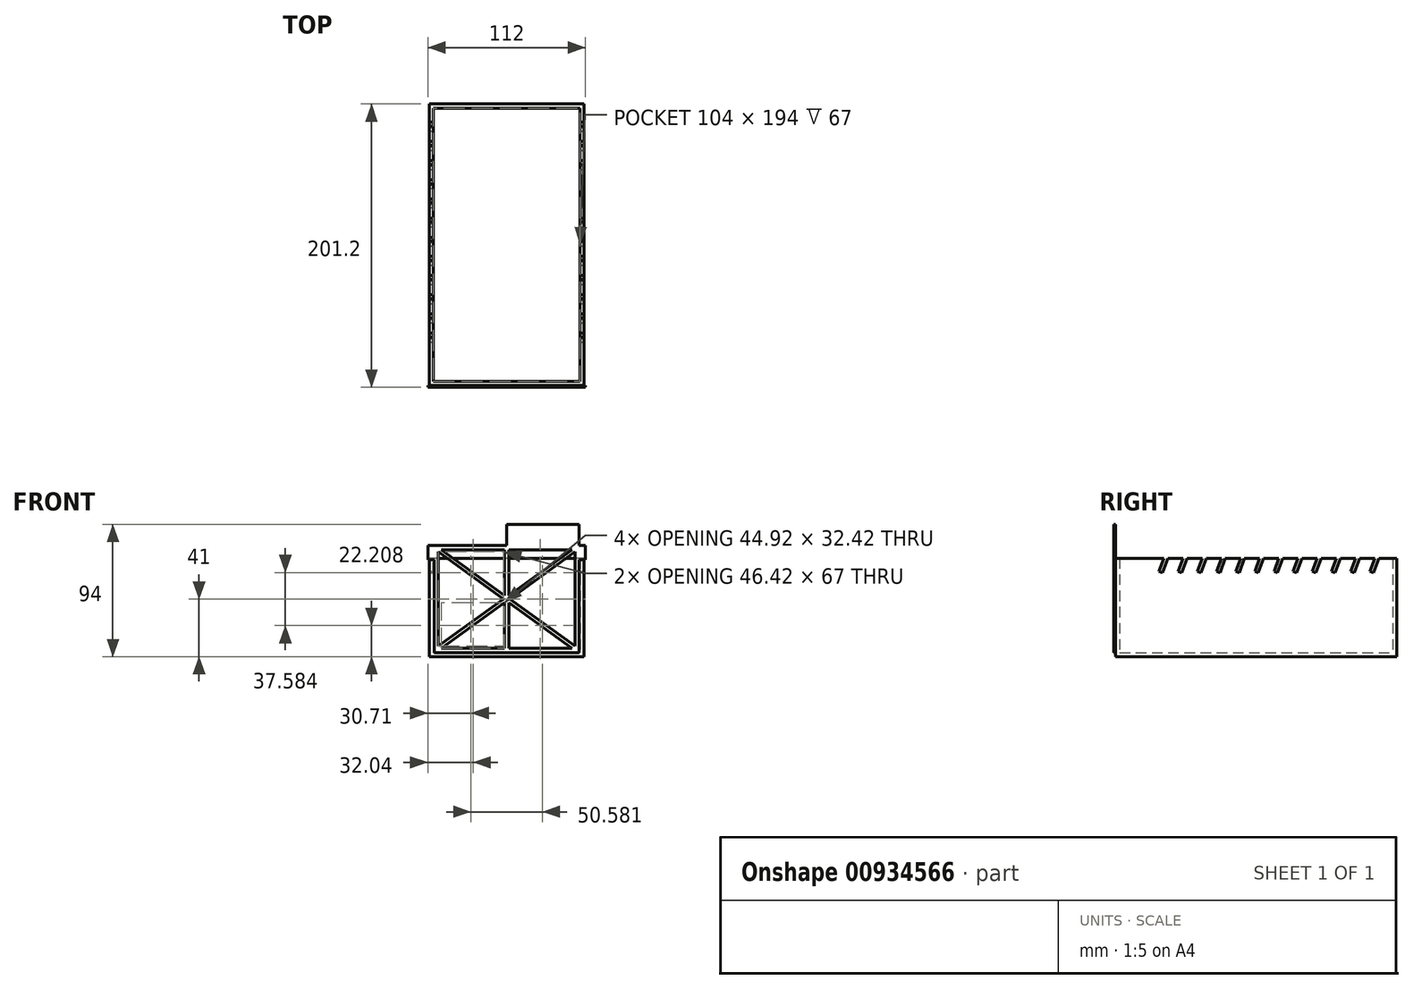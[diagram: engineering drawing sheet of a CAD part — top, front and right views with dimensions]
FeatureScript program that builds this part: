
annotation { "Feature Type Name" : "Feature", "Feature Type Description" : "" }
export const myFeature = defineFeature(function(context is Context, id is Id, definition is map)
    precondition{}
    {
        {
            var Q0;
            Q0=qCreatedBy(makeId("Top.planeOp"),FACE);
            var sketch = newSketch(context, id + "F0", { "sketchPlane" : qUnion([Q0])});
            skLineSegment(sketch, "E0.bottom", {"start": v(0, 0) * mm, "end": v(-110, 0) * mm});
            skLineSegment(sketch, "E0.top", {"start": v(0, 200) * mm, "end": v(-110, 200) * mm});
            skLineSegment(sketch, "E0.left", {"start": v(0, 0) * mm, "end": v(0, 200) * mm});
            skLineSegment(sketch, "E0.right", {"start": v(-110, 0) * mm, "end": v(-110, 200) * mm});
            skSolve(sketch);
        }
        {
            var Q0;
            Q0=makeQuery(id+"F0.imprint","IMPRINT",FACE,{"disambiguationData":[TD([[makeQuery(id+"F0.imprint","IMPRINT",EDGE,{"derivedFrom":sQuery(id+"F0.wireOp",EDGE,"E0.bottom")}),-1.0]])]});
            extrude(context, id + "F1", {"entities" : qUnion([Q0]), "depth" : 70 * mm, "offsetDistance" : 25 * mm});
        }
        {
            var Q0;
            Q0=makeQuery(id+"F1.opExtrude","CAP_FACE",FACE,{"disambiguationData":[OSD([sQuery(id+"F0.wireOp",EDGE,"E0.bottom"),sQuery(id+"F0.wireOp",EDGE,"E0.top"),sQuery(id+"F0.wireOp",EDGE,"E0.left"),sQuery(id+"F0.wireOp",EDGE,"E0.right")])],"isStart":false});
            shell(context, id + "F2", {"entities" : qUnion([Q0]), "thickness" : 3 * mm});
        }
        {
            var Q0;
            Q0=makeQuery(id+"F1.opExtrude","SWEPT_FACE",FACE,{"disambiguationData":[OSD([sQuery(id+"F0.wireOp",EDGE,"E0.bottom")])]});
            var sketch = newSketch(context, id + "F3", { "sketchPlane" : qUnion([Q0])});
            skLineSegment(sketch, "E1.bottom", {"start": v(-106.5, 79) * mm, "end": v(-55, 79) * mm});
            skLineSegment(sketch, "E1.top", {"start": v(-106.5, 3) * mm, "end": v(-3.5, 3) * mm});
            skLineSegment(sketch, "E1.left", {"start": v(-106.5, 69) * mm, "end": v(-106.5, 3) * mm});
            skLineSegment(sketch, "E1.right", {"start": v(-3.5, 69) * mm, "end": v(-3.5, 3) * mm});
            skPoint(sketch, "E2.oppositeSnap0", {"position": v(-55, 79) * mm});
            skLineSegment(sketch, "E2.top", {"start": v(-3.5, 94) * mm, "end": v(-55, 94) * mm});
            skLineSegment(sketch, "E2.left", {"start": v(-3.5, 79) * mm, "end": v(-3.5, 94) * mm});
            skLineSegment(sketch, "E2.right", {"start": v(-55, 79) * mm, "end": v(-55, 94) * mm});
            skLineSegment(sketch, "E3.1", {"start": v(-6.5, 76) * mm, "end": v(-6.5, 6) * mm});
            skLineSegment(sketch, "E3.3", {"start": v(-103.5, 76) * mm, "end": v(-6.5, 76) * mm});
            skLineSegment(sketch, "E3.4", {"start": v(-103.5, 76) * mm, "end": v(-103.5, 6) * mm});
            skLineSegment(sketch, "E3.5", {"start": v(-6.5, 91) * mm, "end": v(-52.5, 91) * mm, "construction": true});
            skLineSegment(sketch, "E3.6", {"start": v(-103.5, 6) * mm, "end": v(-6.5, 6) * mm});
            skLineSegment(sketch, "E4", {"start": v(-103.5, 76) * mm, "end": v(-6.5, 6) * mm, "construction": true});
            skLineSegment(sketch, "E5", {"start": v(-6.5, 76) * mm, "end": v(-103.5, 6) * mm, "construction": true});
            skLineSegment(sketch, "E6.0.left", {"start": v(-6.5, 74.5) * mm, "end": v(-101.42, 6) * mm});
            skLineSegment(sketch, "E6.0.right", {"start": v(-8.58, 76) * mm, "end": v(-103.5, 7.5) * mm});
            skLineSegment(sketch, "E7.0.left", {"start": v(-101.42, 76) * mm, "end": v(-6.5, 7.5) * mm});
            skLineSegment(sketch, "E7.0.right", {"start": v(-103.5, 74.5) * mm, "end": v(-8.58, 6) * mm});
            skLineSegment(sketch, "E8", {"start": v(-55, 76) * mm, "end": v(-55, 6) * mm, "construction": true});
            skLineSegment(sketch, "E9.0.left", {"start": v(-53.5, 76) * mm, "end": v(-53.5, 6) * mm});
            skLineSegment(sketch, "E9.0.right", {"start": v(-56.5, 76) * mm, "end": v(-56.5, 6) * mm});
            skLineSegment(sketch, "E10.bottom", {"start": v(-106.5, 79) * mm, "end": v(-111, 79) * mm});
            skLineSegment(sketch, "E10.top", {"start": v(-106.5, 69) * mm, "end": v(-111, 69) * mm});
            skLineSegment(sketch, "E10.right", {"start": v(-111, 79) * mm, "end": v(-111, 69) * mm});
            skLineSegment(sketch, "E11.MirrorCS", {"start": v(-3.5, 69) * mm, "end": v(1, 69) * mm});
            skLineSegment(sketch, "E12.MirrorCS", {"start": v(-3.5, 79) * mm, "end": v(1, 79) * mm});
            skLineSegment(sketch, "E13.MirrorCS", {"start": v(1, 79) * mm, "end": v(1, 69) * mm});
            skSolve(sketch);
        }
        {
            var Q0;
            Q0=makeQuery(id+"F1.opExtrude","SWEPT_FACE",FACE,{"disambiguationData":[OSD([sQuery(id+"F0.wireOp",EDGE,"E0.left")])]});
            var sketch = newSketch(context, id + "F4", { "sketchPlane" : qUnion([Q0])});
            skLineSegment(sketch, "E14", {"start": v(187, 70) * mm, "end": v(183.24, 59.66) * mm});
            skLineSegment(sketch, "E15", {"start": v(180.8, 60.55) * mm, "end": v(184.23, 70) * mm});
            skLineSegment(sketch, "E16", {"start": v(187, 70) * mm, "end": v(184.23, 70) * mm});
            skLineSegment(sketch, "E17", {"start": v(183.24, 59.66) * mm, "end": v(180.8, 60.55) * mm});
            skLineSegment(sketch, "E18.1.0.0", {"start": v(167.18, 60.55) * mm, "end": v(170.62, 70) * mm});
            skLineSegment(sketch, "E18.1.0.1", {"start": v(173.38, 70) * mm, "end": v(170.62, 70) * mm});
            skLineSegment(sketch, "E18.1.0.2", {"start": v(173.38, 70) * mm, "end": v(169.62, 59.66) * mm});
            skLineSegment(sketch, "E18.1.0.3", {"start": v(169.62, 59.66) * mm, "end": v(167.18, 60.55) * mm});
            skLineSegment(sketch, "E18.2.0.0", {"start": v(153.56, 60.55) * mm, "end": v(157, 70) * mm});
            skLineSegment(sketch, "E18.2.0.1", {"start": v(159.76, 70) * mm, "end": v(157, 70) * mm});
            skLineSegment(sketch, "E18.2.0.2", {"start": v(159.76, 70) * mm, "end": v(156, 59.66) * mm});
            skLineSegment(sketch, "E18.2.0.3", {"start": v(156, 59.66) * mm, "end": v(153.56, 60.55) * mm});
            skLineSegment(sketch, "E18.3.0.0", {"start": v(139.94, 60.55) * mm, "end": v(143.38, 70) * mm});
            skLineSegment(sketch, "E18.3.0.1", {"start": v(146.15, 70) * mm, "end": v(143.38, 70) * mm});
            skLineSegment(sketch, "E18.3.0.2", {"start": v(146.15, 70) * mm, "end": v(142.38, 59.66) * mm});
            skLineSegment(sketch, "E18.3.0.3", {"start": v(142.38, 59.66) * mm, "end": v(139.94, 60.55) * mm});
            skLineSegment(sketch, "E18.4.0.0", {"start": v(126.32, 60.55) * mm, "end": v(129.76, 70) * mm});
            skLineSegment(sketch, "E18.4.0.1", {"start": v(132.53, 70) * mm, "end": v(129.76, 70) * mm});
            skLineSegment(sketch, "E18.4.0.2", {"start": v(132.53, 70) * mm, "end": v(128.77, 59.66) * mm});
            skLineSegment(sketch, "E18.4.0.3", {"start": v(128.77, 59.66) * mm, "end": v(126.32, 60.55) * mm});
            skLineSegment(sketch, "E18.5.0.0", {"start": v(112.7, 60.55) * mm, "end": v(116.14, 70) * mm});
            skLineSegment(sketch, "E18.5.0.1", {"start": v(118.91, 70) * mm, "end": v(116.14, 70) * mm});
            skLineSegment(sketch, "E18.5.0.2", {"start": v(118.91, 70) * mm, "end": v(115.15, 59.66) * mm});
            skLineSegment(sketch, "E18.5.0.3", {"start": v(115.15, 59.66) * mm, "end": v(112.7, 60.55) * mm});
            skLineSegment(sketch, "E18.6.0.0", {"start": v(99.09, 60.55) * mm, "end": v(102.53, 70) * mm});
            skLineSegment(sketch, "E18.6.0.1", {"start": v(105.3, 70) * mm, "end": v(102.53, 70) * mm});
            skLineSegment(sketch, "E18.6.0.2", {"start": v(105.3, 70) * mm, "end": v(101.53, 59.66) * mm});
            skLineSegment(sketch, "E18.6.0.3", {"start": v(101.53, 59.66) * mm, "end": v(99.09, 60.55) * mm});
            skLineSegment(sketch, "E18.direction1", {"start": v(180.8, 60.55) * mm, "end": v(167.18, 60.55) * mm, "construction": true});
            skLineSegment(sketch, "E19.0.7.0", {"start": v(85.47, 60.55) * mm, "end": v(88.9, 70) * mm});
            skLineSegment(sketch, "E19.3.7.0", {"start": v(91.68, 70) * mm, "end": v(88.9, 70) * mm});
            skLineSegment(sketch, "E19.6.7.0", {"start": v(91.68, 70) * mm, "end": v(87.91, 59.66) * mm});
            skLineSegment(sketch, "E19.9.7.0", {"start": v(87.91, 59.66) * mm, "end": v(85.47, 60.55) * mm});
            skLineSegment(sketch, "E19.0.8.0", {"start": v(71.85, 60.55) * mm, "end": v(75.3, 70) * mm});
            skLineSegment(sketch, "E19.3.8.0", {"start": v(78.06, 70) * mm, "end": v(75.3, 70) * mm});
            skLineSegment(sketch, "E19.6.8.0", {"start": v(78.06, 70) * mm, "end": v(74.3, 59.66) * mm});
            skLineSegment(sketch, "E19.9.8.0", {"start": v(74.3, 59.66) * mm, "end": v(71.85, 60.55) * mm});
            skLineSegment(sketch, "E19.0.9.0", {"start": v(58.24, 60.55) * mm, "end": v(61.67, 70) * mm});
            skLineSegment(sketch, "E19.3.9.0", {"start": v(64.44, 70) * mm, "end": v(61.67, 70) * mm});
            skLineSegment(sketch, "E19.6.9.0", {"start": v(64.44, 70) * mm, "end": v(60.68, 59.66) * mm});
            skLineSegment(sketch, "E19.9.9.0", {"start": v(60.68, 59.66) * mm, "end": v(58.24, 60.55) * mm});
            skLineSegment(sketch, "E20.0.10.0", {"start": v(44.62, 60.55) * mm, "end": v(48.06, 70) * mm});
            skLineSegment(sketch, "E20.3.10.0", {"start": v(50.82, 70) * mm, "end": v(48.06, 70) * mm});
            skLineSegment(sketch, "E20.6.10.0", {"start": v(50.82, 70) * mm, "end": v(47.06, 59.66) * mm});
            skLineSegment(sketch, "E20.9.10.0", {"start": v(47.06, 59.66) * mm, "end": v(44.62, 60.55) * mm});
            skLineSegment(sketch, "E20.0.11.0", {"start": v(31, 60.55) * mm, "end": v(34.44, 70) * mm});
            skLineSegment(sketch, "E20.3.11.0", {"start": v(37.2, 70) * mm, "end": v(34.44, 70) * mm});
            skLineSegment(sketch, "E20.6.11.0", {"start": v(37.2, 70) * mm, "end": v(33.44, 59.66) * mm});
            skLineSegment(sketch, "E20.9.11.0", {"start": v(33.44, 59.66) * mm, "end": v(31, 60.55) * mm});
            skSolve(sketch);
        }
        {
            var Q0;
            Q0 = qSketchRegion(id + "F4", true);
            extrude(context, id + "F5", {"entities" : qUnion([Q0]), "operationType" : NewBodyOperationType.REMOVE, "endBound" : BoundingType.THROUGH_ALL, "oppositeDirection" : true, "depth" : 25 * mm, "offsetDistance" : 25 * mm});
        }
        {
            var Q0;
            {var subQ9=sQuery(id+"F3.wireOp",EDGE,"E1.bottom");Q0=makeQuery(id+"F3.imprint","IMPRINT",FACE,{"disambiguationData":[TD([[makeQuery(id+"F3.imprint","IMPRINT",EDGE,{"derivedFrom":subQ9}),-1.0]])]});}
            var Q1;
            {var subQ3=sQuery(id+"F3.wireOp",EDGE,"E1.top");Q1=makeQuery(id+"F3.imprint","IMPRINT",FACE,{"disambiguationData":[TD([[makeQuery(id+"F3.imprint","IMPRINT",EDGE,{"derivedFrom":subQ3}),1.0]])]});}
            var Q2;
            {var subQ1=sQuery(id+"F3.wireOp",EDGE,"E3.4");var subQ6=sQuery(id+"F3.wireOp",EDGE,"E3.6");var subQ10=makeQuery(id+"F3.imprint","INTERSECT",VERTEX,{"derivedFrom":[subQ1,subQ6]});Q2=makeQuery(id+"F3.imprint","IMPRINT",FACE,{"disambiguationData":[TD([[makeQuery(id+"F3.imprint","IMPRINT",EDGE,{"disambiguationData":[TD([[subQ10,1.0]])],"derivedFrom":subQ1}),1.0]])]});}
            var Q3;
            {var subQ0=sQuery(id+"F3.wireOp",EDGE,"E7.0.left");var subQ1=sQuery(id+"F3.wireOp",EDGE,"E6.0.right");var subQ2=makeQuery(id+"F3.imprint","INTERSECT",VERTEX,{"derivedFrom":[subQ1,subQ0]});Q3=makeQuery(id+"F3.imprint","IMPRINT",FACE,{"disambiguationData":[TD([[makeQuery(id+"F3.imprint","IMPRINT",EDGE,{"disambiguationData":[TD([[subQ2,-1.0]])],"derivedFrom":subQ1}),-1.0]])]});}
            var Q4;
            {var subQ5=sQuery(id+"F3.wireOp",EDGE,"E7.0.left");var subQ7=sQuery(id+"F3.wireOp",EDGE,"E6.0.left");var subQ8=makeQuery(id+"F3.imprint","INTERSECT",VERTEX,{"derivedFrom":[subQ7,subQ5]});Q4=makeQuery(id+"F3.imprint","IMPRINT",FACE,{"disambiguationData":[TD([[makeQuery(id+"F3.imprint","IMPRINT",EDGE,{"disambiguationData":[TD([[subQ8,1.0]])],"derivedFrom":subQ7}),-1.0]])]});}
            var Q5;
            {var subQ0=sQuery(id+"F3.wireOp",EDGE,"E7.0.left");var subQ1=sQuery(id+"F3.wireOp",EDGE,"E6.0.left");var subQ2=makeQuery(id+"F3.imprint","INTERSECT",VERTEX,{"derivedFrom":[subQ1,subQ0]});Q5=makeQuery(id+"F3.imprint","IMPRINT",FACE,{"disambiguationData":[TD([[makeQuery(id+"F3.imprint","IMPRINT",EDGE,{"disambiguationData":[TD([[subQ2,-1.0]])],"derivedFrom":subQ1}),-1.0]])]});}
            var Q6;
            {var subQ1=sQuery(id+"F3.wireOp",EDGE,"E3.1");var subQ9=sQuery(id+"F3.wireOp",EDGE,"E3.6");var subQ10=makeQuery(id+"F3.imprint","INTERSECT",VERTEX,{"derivedFrom":[subQ1,subQ9]});Q6=makeQuery(id+"F3.imprint","IMPRINT",FACE,{"disambiguationData":[TD([[makeQuery(id+"F3.imprint","IMPRINT",EDGE,{"disambiguationData":[TD([[subQ10,1.0]])],"derivedFrom":subQ1}),-1.0]])]});}
            var Q7;
            {var subQ1=sQuery(id+"F3.wireOp",EDGE,"E3.3");var subQ6=sQuery(id+"F3.wireOp",EDGE,"E3.1");var subQ9=makeQuery(id+"F3.imprint","INTERSECT",VERTEX,{"derivedFrom":[subQ6,subQ1]});Q7=makeQuery(id+"F3.imprint","IMPRINT",FACE,{"disambiguationData":[TD([[makeQuery(id+"F3.imprint","IMPRINT",EDGE,{"disambiguationData":[TD([[subQ9,-1.0]])],"derivedFrom":subQ6}),-1.0]])]});}
            var Q8;
            {var subQ1=sQuery(id+"F3.wireOp",EDGE,"E3.4");var subQ6=sQuery(id+"F3.wireOp",EDGE,"E3.3");var subQ9=makeQuery(id+"F3.imprint","INTERSECT",VERTEX,{"derivedFrom":[subQ6,subQ1]});Q8=makeQuery(id+"F3.imprint","IMPRINT",FACE,{"disambiguationData":[TD([[makeQuery(id+"F3.imprint","IMPRINT",EDGE,{"disambiguationData":[TD([[subQ9,-1.0]])],"derivedFrom":subQ6}),-1.0]])]});}
            var Q9;
            {var subQ0=sQuery(id+"F3.wireOp",EDGE,"E9.0.right");var subQ1=sQuery(id+"F3.wireOp",EDGE,"E6.0.right");var subQ2=makeQuery(id+"F3.imprint","INTERSECT",VERTEX,{"derivedFrom":[subQ1,subQ0]});Q9=makeQuery(id+"F3.imprint","IMPRINT",FACE,{"disambiguationData":[TD([[makeQuery(id+"F3.imprint","IMPRINT",EDGE,{"disambiguationData":[TD([[subQ2,-1.0]])],"derivedFrom":subQ1}),-1.0]])]});}
            var Q10;
            {var subQ5=sQuery(id+"F3.wireOp",EDGE,"E9.0.left");var subQ6=sQuery(id+"F3.wireOp",EDGE,"E6.0.right");var subQ7=makeQuery(id+"F3.imprint","INTERSECT",VERTEX,{"derivedFrom":[subQ6,subQ5]});Q10=makeQuery(id+"F3.imprint","IMPRINT",FACE,{"disambiguationData":[TD([[makeQuery(id+"F3.imprint","IMPRINT",EDGE,{"disambiguationData":[TD([[subQ7,-1.0]])],"derivedFrom":subQ6}),-1.0]])]});}
            var Q11;
            {var subQ0=sQuery(id+"F3.wireOp",EDGE,"E9.0.left");var subQ1=sQuery(id+"F3.wireOp",EDGE,"E3.3");var subQ2=makeQuery(id+"F3.imprint","INTERSECT",VERTEX,{"derivedFrom":[subQ1,subQ0]});Q11=makeQuery(id+"F3.imprint","IMPRINT",FACE,{"disambiguationData":[TD([[makeQuery(id+"F3.imprint","IMPRINT",EDGE,{"disambiguationData":[TD([[subQ2,1.0]])],"derivedFrom":subQ1}),-1.0]])]});}
            var Q12;
            {var subQ0=sQuery(id+"F3.wireOp",EDGE,"E9.0.left");var subQ1=sQuery(id+"F3.wireOp",EDGE,"E3.6");var subQ2=makeQuery(id+"F3.imprint","INTERSECT",VERTEX,{"derivedFrom":[subQ1,subQ0]});Q12=makeQuery(id+"F3.imprint","IMPRINT",FACE,{"disambiguationData":[TD([[makeQuery(id+"F3.imprint","IMPRINT",EDGE,{"disambiguationData":[TD([[subQ2,1.0]])],"derivedFrom":subQ1}),1.0]])]});}
            var Q13;
            {var subQ1=sQuery(id+"F3.wireOp",EDGE,"E6.0.left");var subQ8=sQuery(id+"F3.wireOp",EDGE,"E9.0.left");var subQ11=makeQuery(id+"F3.imprint","INTERSECT",VERTEX,{"derivedFrom":[subQ1,subQ8]});Q13=makeQuery(id+"F3.imprint","IMPRINT",FACE,{"disambiguationData":[TD([[makeQuery(id+"F3.imprint","IMPRINT",EDGE,{"disambiguationData":[TD([[subQ11,-1.0]])],"derivedFrom":subQ1}),-1.0]])]});}
            var Q14;
            {var subQ0=sQuery(id+"F3.wireOp",EDGE,"E9.0.left");var subQ1=sQuery(id+"F3.wireOp",EDGE,"E6.0.left");var subQ2=makeQuery(id+"F3.imprint","INTERSECT",VERTEX,{"derivedFrom":[subQ1,subQ0]});Q14=makeQuery(id+"F3.imprint","IMPRINT",FACE,{"disambiguationData":[TD([[makeQuery(id+"F3.imprint","IMPRINT",EDGE,{"disambiguationData":[TD([[subQ2,-1.0]])],"derivedFrom":subQ1}),1.0]])]});}
            var Q15;
            {var subQ0=sQuery(id+"F3.wireOp",EDGE,"E9.0.left");var subQ1=sQuery(id+"F3.wireOp",EDGE,"E6.0.right");var subQ2=makeQuery(id+"F3.imprint","INTERSECT",VERTEX,{"derivedFrom":[subQ1,subQ0]});Q15=makeQuery(id+"F3.imprint","IMPRINT",FACE,{"disambiguationData":[TD([[makeQuery(id+"F3.imprint","IMPRINT",EDGE,{"disambiguationData":[TD([[subQ2,-1.0]])],"derivedFrom":subQ1}),1.0]])]});}
            var Q16;
            {var subQ0=sQuery(id+"F3.wireOp",EDGE,"E7.0.right");var subQ1=sQuery(id+"F3.wireOp",EDGE,"E6.0.left");var subQ2=makeQuery(id+"F3.imprint","INTERSECT",VERTEX,{"derivedFrom":[subQ1,subQ0]});Q16=makeQuery(id+"F3.imprint","IMPRINT",FACE,{"disambiguationData":[TD([[makeQuery(id+"F3.imprint","IMPRINT",EDGE,{"disambiguationData":[TD([[subQ2,-1.0]])],"derivedFrom":subQ1}),-1.0]])]});}
            var Q17;
            {var subQ0=sQuery(id+"F3.wireOp",EDGE,"E9.0.right");var subQ1=sQuery(id+"F3.wireOp",EDGE,"E6.0.right");var subQ2=makeQuery(id+"F3.imprint","INTERSECT",VERTEX,{"derivedFrom":[subQ1,subQ0]});Q17=makeQuery(id+"F3.imprint","IMPRINT",FACE,{"disambiguationData":[TD([[makeQuery(id+"F3.imprint","IMPRINT",EDGE,{"disambiguationData":[TD([[subQ2,-1.0]])],"derivedFrom":subQ1}),1.0]])]});}
            extrude(context, id + "F6", {"entities" : qUnion([Q0, Q1, Q2, Q3, Q4, Q5, Q6, Q7, Q8, Q9, Q10, Q11, Q12, Q13, Q14, Q15, Q16, Q17]), "depth" : 1.2 * mm, "offsetDistance" : 25 * mm});
        }
    });
